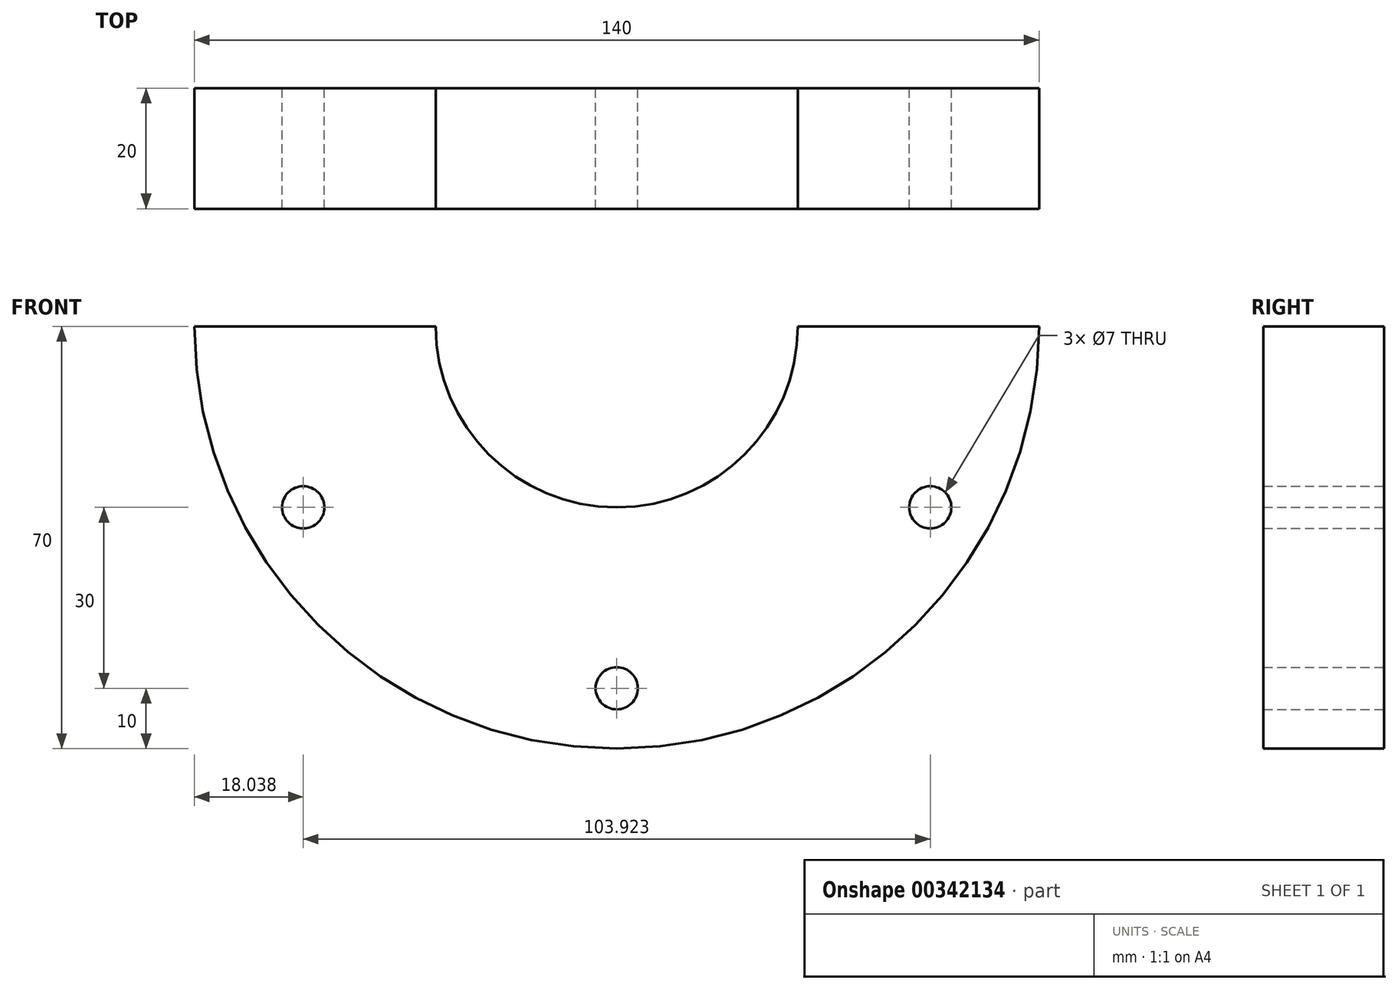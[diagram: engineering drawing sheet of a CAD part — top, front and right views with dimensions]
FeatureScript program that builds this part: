
annotation { "Feature Type Name" : "Feature", "Feature Type Description" : "" }
export const myFeature = defineFeature(function(context is Context, id is Id, definition is map)
    precondition{}
    {
        {
            var Q0;
            Q0=qCreatedBy(makeId("Front.planeOp"),FACE);
            var sketch = newSketch(context, id + "F0", { "sketchPlane" : qUnion([Q0])});
            skLineSegment(sketch, "E0", {"start": v(70, 0) * mm, "end": v(30, 0) * mm});
            skArc(sketch, "E1", {"start": v(-70, 0) * mm, "mid": v(0, -70) * mm, "end": v(70, 0) * mm});
            skCircle(sketch, "E2.MirrorC", {"center": v(-51.96, -30) * mm, "radius": 3.5 * mm});
            skArc(sketch, "E3", {"start": v(-60, 0) * mm, "mid": v(0, -60) * mm, "end": v(60, 0) * mm, "construction": true});
            skArc(sketch, "E4", {"start": v(-30, 0) * mm, "mid": v(0, -30) * mm, "end": v(30, 0) * mm});
            skLineSegment(sketch, "E5", {"start": v(0, 0) * mm, "end": v(0, -70) * mm, "construction": true});
            skCircle(sketch, "E6", {"center": v(0, -60) * mm, "radius": 3.5 * mm});
            skCircle(sketch, "E7.1.0", {"center": v(51.96, -30) * mm, "radius": 3.5 * mm});
            skLineSegment(sketch, "E8.trimOffspring", {"start": v(-30, 0) * mm, "end": v(-70, 0) * mm});
            skSolve(sketch);
        }
        {
            var Q0;
            Q0=qSketchRegion(id+"F0",true);
            extrude(context, id + "F1", {"entities" : qUnion([Q0]), "depth" : 20 * mm});
        }
    });
